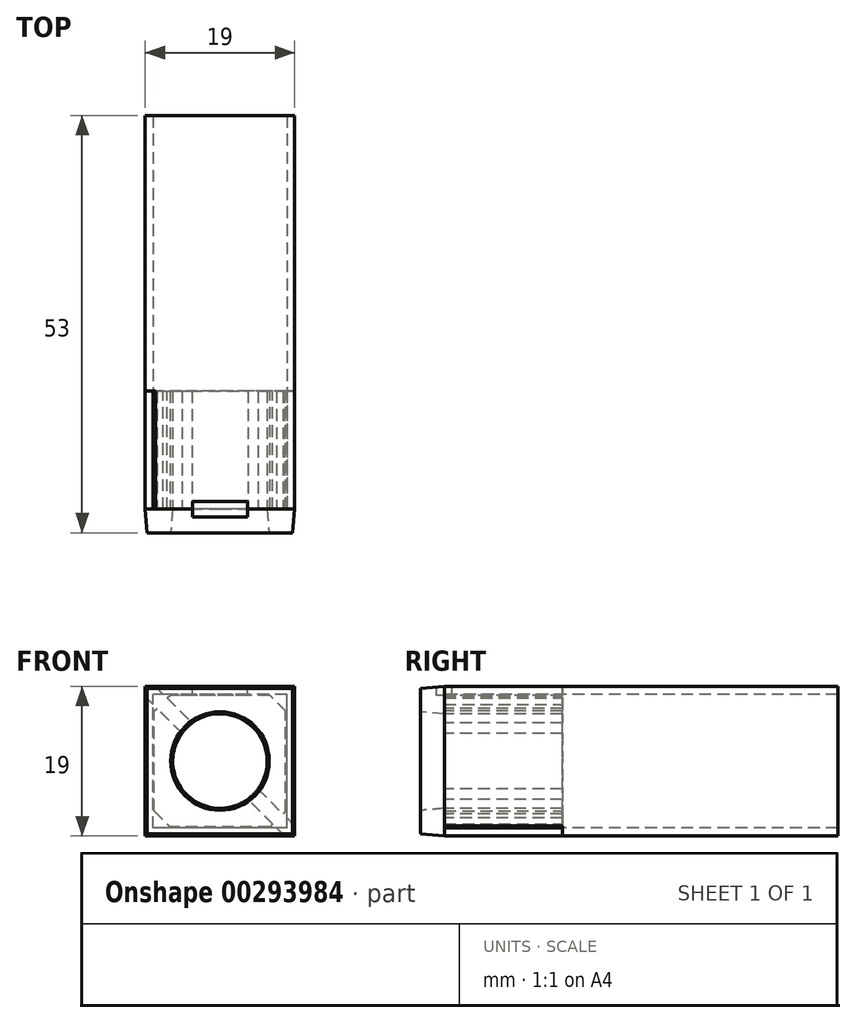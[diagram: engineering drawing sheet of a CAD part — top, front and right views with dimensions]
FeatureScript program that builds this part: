
annotation { "Feature Type Name" : "Feature", "Feature Type Description" : "" }
export const myFeature = defineFeature(function(context is Context, id is Id, definition is map)
    precondition{}
    {
        {
            var Q0;
            Q0=qCreatedBy(makeId("Front.planeOp"),FACE);
            var sketch = newSketch(context, id + "F0", { "sketchPlane" : qUnion([Q0])});
            skLineSegment(sketch, "E0.bottom", {"start": v(8.5, -8.5) * mm, "end": v(-8.5, -8.5) * mm});
            skLineSegment(sketch, "E0.top", {"start": v(8.5, 8.5) * mm, "end": v(-8.5, 8.5) * mm});
            skLineSegment(sketch, "E0.left", {"start": v(8.5, -8.5) * mm, "end": v(8.5, 8.5) * mm});
            skLineSegment(sketch, "E0.right", {"start": v(-8.5, -8.5) * mm, "end": v(-8.5, 8.5) * mm});
            skPoint(sketch, "E0.middle", {"position": v(0, 0) * mm});
            skLineSegment(sketch, "E1.0", {"start": v(9.5, 9.5) * mm, "end": v(-9.5, 9.5) * mm});
            skLineSegment(sketch, "E1.1", {"start": v(9.5, -9.5) * mm, "end": v(9.5, 9.5) * mm});
            skLineSegment(sketch, "E1.2", {"start": v(9.5, -9.5) * mm, "end": v(-9.5, -9.5) * mm});
            skLineSegment(sketch, "E1.3", {"start": v(-9.5, -9.5) * mm, "end": v(-9.5, 9.5) * mm});
            skSolve(sketch);
        }
        {
            var Q0;
            Q0=qSketchRegion(id+"F0",true);
            extrude(context, id + "F1", {"entities" : qUnion([Q0]), "oppositeDirection" : true, "depth" : 50 * mm});
        }
        {
            var Q0;
            Q0=makeQuery(id+"F1.opExtrude","CAP_FACE",FACE,{"disambiguationData":[OSD([sQuery(id+"F0.wireOp",EDGE,"E0.bottom"),sQuery(id+"F0.wireOp",EDGE,"E0.top"),sQuery(id+"F0.wireOp",EDGE,"E0.left"),sQuery(id+"F0.wireOp",EDGE,"E0.right"),sQuery(id+"F0.wireOp",EDGE,"E1.0"),sQuery(id+"F0.wireOp",EDGE,"E1.1"),sQuery(id+"F0.wireOp",EDGE,"E1.2"),sQuery(id+"F0.wireOp",EDGE,"E1.3")])],"isStart":true});
            var sketch = newSketch(context, id + "F2", { "sketchPlane" : qUnion([Q0])});
            skLineSegment(sketch, "E2.0", {"start": v(8.35, 8.35) * mm, "end": v(-8.35, 8.35) * mm});
            skLineSegment(sketch, "E2.1", {"start": v(8.35, -8.35) * mm, "end": v(8.35, 8.35) * mm});
            skLineSegment(sketch, "E2.2", {"start": v(8.35, -8.35) * mm, "end": v(-8.35, -8.35) * mm});
            skLineSegment(sketch, "E2.3", {"start": v(-8.35, -8.35) * mm, "end": v(-8.35, 8.35) * mm});
            skCircle(sketch, "E3", {"center": v(0, 0) * mm, "radius": 6 * mm});
            skSolve(sketch);
        }
        {
            var Q0;
            Q0=qSketchRegion(id+"F2",true);
            extrude(context, id + "F3", {"entities" : qUnion([Q0]), "oppositeDirection" : true, "depth" : 15 * mm});
        }
        {
            var Q0;
            Q0=makeQuery(id+"F3.opExtrude","CAP_FACE",FACE,{"disambiguationData":[OSD([sQuery(id+"F2.wireOp",EDGE,"E2.0"),sQuery(id+"F2.wireOp",EDGE,"E2.1"),sQuery(id+"F2.wireOp",EDGE,"E2.2"),sQuery(id+"F2.wireOp",EDGE,"E2.3"),sQuery(id+"F2.wireOp",EDGE,"E3")])],"isStart":true});
            var sketch = newSketch(context, id + "F4", { "sketchPlane" : qUnion([Q0])});
            skLineSegment(sketch, "E4.0.0", {"start": v(-9.5, 9.5) * mm, "end": v(-9.5, -9.5) * mm});
            skLineSegment(sketch, "E4.0.1", {"start": v(-9.5, -9.5) * mm, "end": v(9.5, -9.5) * mm});
            skLineSegment(sketch, "E4.0.2", {"start": v(9.5, -9.5) * mm, "end": v(9.5, 9.5) * mm});
            skLineSegment(sketch, "E4.0.3", {"start": v(9.5, 9.5) * mm, "end": v(-9.5, 9.5) * mm});
            skCircle(sketch, "E5.0", {"center": v(0, 0) * mm, "radius": 6 * mm});
            skSolve(sketch);
        }
        {
            var Q0;
            Q0=qSketchRegion(id+"F4",true);
            extrude(context, id + "F5", {"entities" : qUnion([Q0]), "operationType" : NewBodyOperationType.ADD, "depth" : 3 * mm, "hasDraft" : true, "draftAngle" : 5 * degree, "draftPullDirection" : true});
        }
        {
            var Q0;
            Q0=makeQuery(id+"F1.opExtrude","SWEPT_FACE",FACE,{"disambiguationData":[OSD([sQuery(id+"F0.wireOp",EDGE,"E1.0")])]});
            var sketch = newSketch(context, id + "F6", { "sketchPlane" : qUnion([Q0])});
            skLineSegment(sketch, "E6.bottom", {"start": v(3.5, 1) * mm, "end": v(-3.5, 1) * mm});
            skLineSegment(sketch, "E6.top", {"start": v(3.5, -1) * mm, "end": v(-3.5, -1) * mm});
            skLineSegment(sketch, "E6.left", {"start": v(3.5, 1) * mm, "end": v(3.5, -1) * mm});
            skLineSegment(sketch, "E6.right", {"start": v(-3.5, 1) * mm, "end": v(-3.5, -1) * mm});
            skPoint(sketch, "E6.middle", {"position": v(0, 0) * mm});
            skSolve(sketch);
        }
        {
            var Q0;
            {var subQ0=sQuery(id+"F6.wireOp",EDGE,"E6.top");Q0=makeQuery(id+"F6.imprint","IMPRINT",FACE,{"disambiguationData":[TD([[makeQuery(id+"F6.imprint","IMPRINT",EDGE,{"derivedFrom":subQ0}),-1.0]])]});}
            var Q1;
            {var subQ0=sQuery(id+"F6.wireOp",EDGE,"E6.bottom");Q1=makeQuery(id+"F6.imprint","IMPRINT",FACE,{"disambiguationData":[TD([[makeQuery(id+"F6.imprint","IMPRINT",EDGE,{"derivedFrom":subQ0}),1.0]])]});}
            var Q2;
            Q2=makeQuery(id+"F3.opExtrude","SWEPT_FACE",FACE,{"disambiguationData":[OSD([sQuery(id+"F2.wireOp",EDGE,"E2.0")])]});
            extrude(context, id + "F7", {"entities" : qUnion([Q0, Q1]), "operationType" : NewBodyOperationType.REMOVE, "oppositeDirection" : true, "endBoundEntityFace" : qUnion([Q2]), "depth" : 1.15 * mm});
        }
        {
            var Q0;
            Q0=makeQuery(id+"F3.opExtrude","SWEPT_EDGE",EDGE,{"disambiguationData":[OSD([sQuery(id+"F2.wireOp",EDGE,"E2.0"),sQuery(id+"F2.wireOp",EDGE,"E2.1")])]});
            var Q1;
            Q1=makeQuery(id+"F3.opExtrude","SWEPT_EDGE",EDGE,{"disambiguationData":[OSD([sQuery(id+"F2.wireOp",EDGE,"E2.1"),sQuery(id+"F2.wireOp",EDGE,"E2.2")])]});
            var Q2;
            Q2=makeQuery(id+"F3.opExtrude","SWEPT_EDGE",EDGE,{"disambiguationData":[OSD([sQuery(id+"F2.wireOp",EDGE,"E2.2"),sQuery(id+"F2.wireOp",EDGE,"E2.3")])]});
            var Q3;
            Q3=makeQuery(id+"F3.opExtrude","SWEPT_EDGE",EDGE,{"disambiguationData":[OSD([sQuery(id+"F2.wireOp",EDGE,"E2.0"),sQuery(id+"F2.wireOp",EDGE,"E2.3")])]});
            chamfer(context, id + "F8", {"entities" : qUnion([Q0, Q1, Q2, Q3]), "width" : 2 * mm, "tangentPropagation" : true});
        }
        {
            var Q0;
            Q0=makeQuery(id+"F3.opExtrude","CAP_FACE",FACE,{"disambiguationData":[OSD([sQuery(id+"F2.wireOp",EDGE,"E2.0"),sQuery(id+"F2.wireOp",EDGE,"E2.1"),sQuery(id+"F2.wireOp",EDGE,"E2.2"),sQuery(id+"F2.wireOp",EDGE,"E2.3"),sQuery(id+"F2.wireOp",EDGE,"E3")])],"isStart":false});
            var sketch = newSketch(context, id + "F9", { "sketchPlane" : qUnion([Q0])});
            skLineSegment(sketch, "E7", {"start": v(12.79, 14.79) * mm, "end": v(-12.4, -10.4) * mm});
            skLineSegment(sketch, "E8", {"start": v(-12.4, -10.4) * mm, "end": v(-10.4, -12.4) * mm});
            skLineSegment(sketch, "E9", {"start": v(-10.4, -12.4) * mm, "end": v(14.65, 12.65) * mm});
            skLineSegment(sketch, "E10", {"start": v(14.65, 12.65) * mm, "end": v(12.79, 14.79) * mm});
            skLineSegment(sketch, "E11.0", {"start": v(12.76, 14.06) * mm, "end": v(-11.7, -10.4) * mm});
            skLineSegment(sketch, "E11.1", {"start": v(13.97, 12.67) * mm, "end": v(12.76, 14.06) * mm});
            skLineSegment(sketch, "E11.2", {"start": v(-10.4, -11.7) * mm, "end": v(13.97, 12.67) * mm});
            skLineSegment(sketch, "E11.3", {"start": v(-11.7, -10.4) * mm, "end": v(-10.4, -11.7) * mm});
            skSolve(sketch);
        }
        {
            var Q0;
            {var subQ0=sQuery(id+"F9.wireOp",EDGE,"E11.1");Q0=makeQuery(id+"F9.imprint","IMPRINT",FACE,{"disambiguationData":[TD([[makeQuery(id+"F9.imprint","IMPRINT",EDGE,{"derivedFrom":subQ0}),1.0]])]});}
            var Q1;
            {var subQ0=sQuery(id+"F9.wireOp",EDGE,"E11.0");var subQ1=sQuery(id+"F2.wireOp",EDGE,"E3");var subQ6=makeQuery(id+"F3.opExtrude","CAP_EDGE",EDGE,{"disambiguationData":[OSD([subQ1])],"isStart":false});var subQ7=makeQuery(id+"F9.imprint","INTERSECT",VERTEX,{"disambiguationData":[OD(0.0)],"derivedFrom":[subQ6,subQ0]});Q1=makeQuery(id+"F9.imprint","IMPRINT",FACE,{"disambiguationData":[TD([[makeQuery(id+"F9.imprint","IMPRINT",EDGE,{"disambiguationData":[TD([[subQ7,-1.0]])],"derivedFrom":subQ6}),1.0]])]});}
            var Q2;
            {var subQ0=sQuery(id+"F9.wireOp",EDGE,"E11.3");Q2=makeQuery(id+"F9.imprint","IMPRINT",FACE,{"disambiguationData":[TD([[makeQuery(id+"F9.imprint","IMPRINT",EDGE,{"derivedFrom":subQ0}),1.0]])]});}
            var Q3;
            {var subQ0=sQuery(id+"F9.wireOp",EDGE,"E11.0");var subQ1=makeQuery(id+"F3.opExtrude","CAP_EDGE",EDGE,{"disambiguationData":[OSD([sQuery(id+"F2.wireOp",EDGE,"E3")])],"isStart":false});var subQ2=makeQuery(id+"F9.imprint","INTERSECT",VERTEX,{"disambiguationData":[OD(0.0)],"derivedFrom":[subQ1,subQ0]});Q3=makeQuery(id+"F9.imprint","IMPRINT",FACE,{"disambiguationData":[TD([[makeQuery(id+"F9.imprint","IMPRINT",EDGE,{"disambiguationData":[TD([[subQ2,-1.0]])],"derivedFrom":subQ0}),1.0]])]});}
            var Q4;
            {var subQ0=sQuery(id+"F9.wireOp",EDGE,"E11.0");var subQ1=sQuery(id+"F2.wireOp",EDGE,"E3");var subQ2=makeQuery(id+"F3.opExtrude","CAP_EDGE",EDGE,{"disambiguationData":[OSD([subQ1])],"isStart":false});var subQ3=makeQuery(id+"F9.imprint","INTERSECT",VERTEX,{"disambiguationData":[OD(1.0)],"derivedFrom":[subQ2,subQ0]});Q4=makeQuery(id+"F9.imprint","IMPRINT",FACE,{"disambiguationData":[TD([[makeQuery(id+"F9.imprint","IMPRINT",EDGE,{"disambiguationData":[TD([[subQ3,1.0]])],"derivedFrom":subQ2}),1.0]])]});}
            var Q5;
            {var subQ0=sQuery(id+"F4.wireOp",EDGE,"E4.0.3");var subQ2=sQuery(id+"F4.wireOp",EDGE,"E4.0.0");var subQ5=makeQuery(id+"F3.opExtrude","SWEPT_FACE",FACE,{"disambiguationData":[OSD([sQuery(id+"F2.wireOp",EDGE,"E2.0")])]});var subQ12=makeQuery(id+"F3.opExtrude","SWEPT_FACE",FACE,{"disambiguationData":[OSD([sQuery(id+"F2.wireOp",EDGE,"E2.2")])]});var subQ13=sQuery(id+"F4.wireOp",EDGE,"E4.0.1");var subQ15=sQuery(id+"F4.wireOp",EDGE,"E4.0.2");Q5=makeQuery(id+"FJbmcXwFBvmhBgo_2.3.F7.boolean.opBoolean","SPLIT",FACE,{"disambiguationData":[TD([subQ5])],"derivedFrom":makeQuery(id+"FJbmcXwFBvmhBgo_2.2.F7.boolean.opBoolean","SPLIT",FACE,{"disambiguationData":[TD([subQ5])],"derivedFrom":makeQuery(id+"FJbmcXwFBvmhBgo_2.1.F7.boolean.opBoolean","SPLIT",FACE,{"disambiguationData":[TD([subQ12])],"derivedFrom":makeQuery(id+"F5.opExtrude","CAP_FACE",FACE,{"disambiguationData":[OSD([subQ2,subQ13,subQ15,subQ0,sQuery(id+"F4.wireOp",EDGE,"E5.0")])],"isStart":true})})})});}
            extrude(context, id + "F10", {"entities" : qUnion([Q0, Q1, Q2, Q3, Q4]), "operationType" : NewBodyOperationType.REMOVE, "endBound" : BoundingType.UP_TO_SURFACE, "oppositeDirection" : true, "endBoundEntityFace" : qUnion([Q5]), "depth" : 25 * mm});
        }
    });
